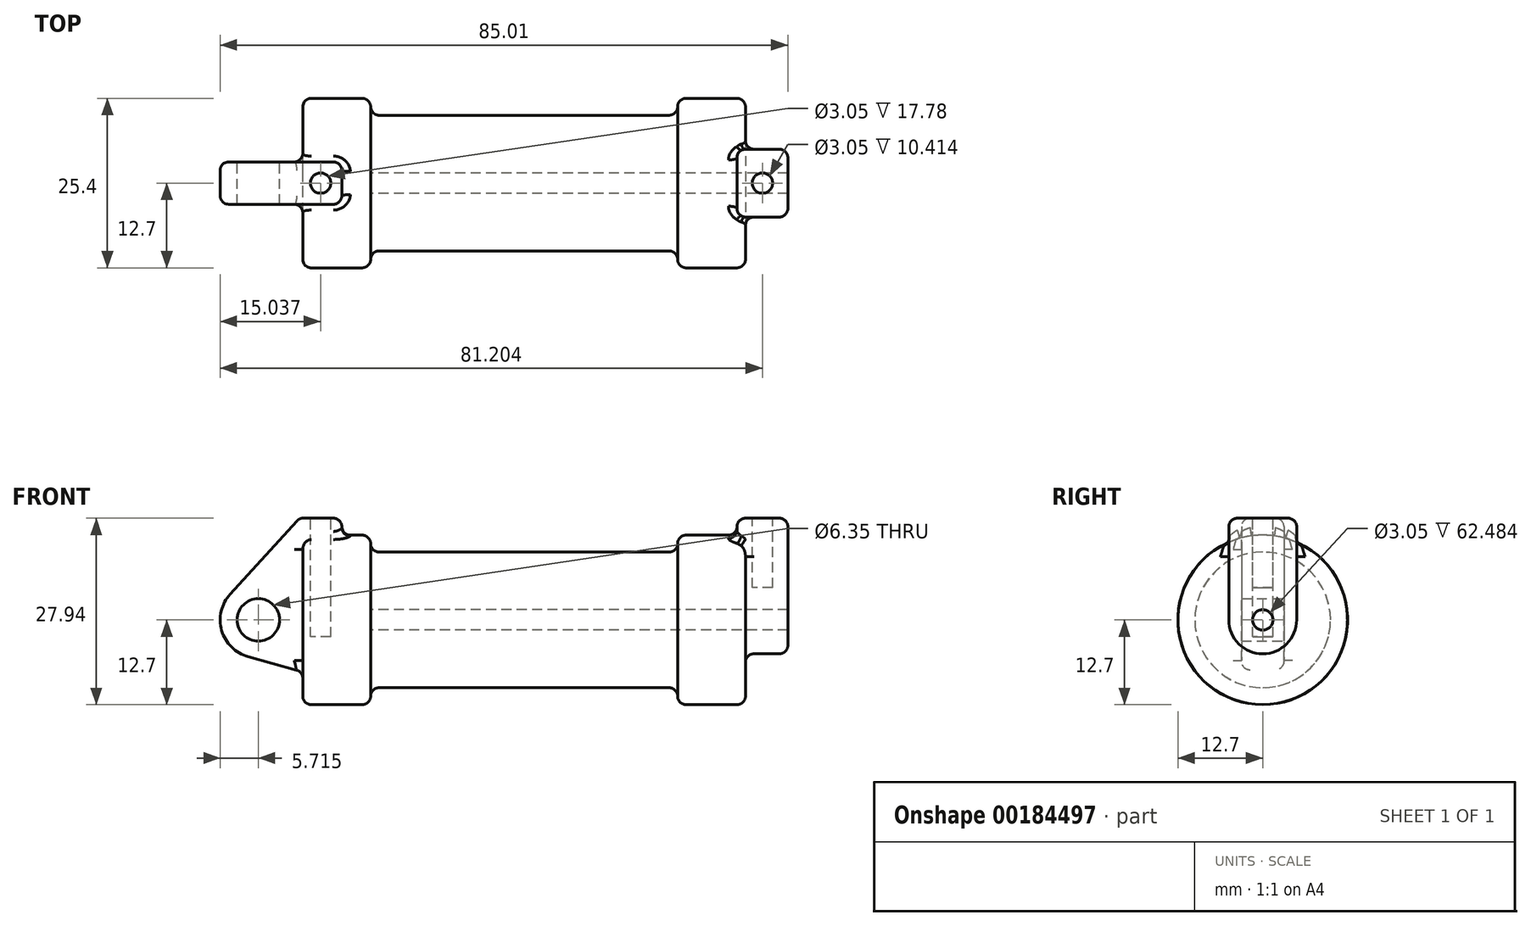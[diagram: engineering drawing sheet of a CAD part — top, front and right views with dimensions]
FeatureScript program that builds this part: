
annotation { "Feature Type Name" : "Feature", "Feature Type Description" : "" }
export const myFeature = defineFeature(function(context is Context, id is Id, definition is map)
    precondition{}
    {
        {
            var Q0;
            Q0=qCreatedBy(makeId("Front.planeOp"),FACE);
            var sketch = newSketch(context, id + "F0", { "sketchPlane" : qUnion([Q0])});
            skLineSegment(sketch, "E0", {"start": v(0, 0) * mm, "end": v(0, 12.7) * mm});
            skLineSegment(sketch, "E1", {"start": v(0, 12.7) * mm, "end": v(10.16, 12.7) * mm});
            skLineSegment(sketch, "E2", {"start": v(10.16, 12.7) * mm, "end": v(10.16, 10.16) * mm});
            skLineSegment(sketch, "E3", {"start": v(10.16, 10.16) * mm, "end": v(56.13, 10.16) * mm});
            skLineSegment(sketch, "E4", {"start": v(56.13, 10.16) * mm, "end": v(56.13, 12.7) * mm});
            skLineSegment(sketch, "E5", {"start": v(56.13, 12.7) * mm, "end": v(66.3, 12.7) * mm});
            skLineSegment(sketch, "E6", {"start": v(66.3, 12.7) * mm, "end": v(66.3, 0) * mm});
            skLineSegment(sketch, "E7", {"start": v(66.3, 0) * mm, "end": v(0, 0) * mm});
            skLineSegment(sketch, "E8", {"start": v(5.84, 15.24) * mm, "end": v(-0.5, 15.24) * mm});
            skLineSegment(sketch, "E9", {"start": v(-0.5, 15.24) * mm, "end": v(-10.88, 3.85) * mm});
            skLineSegment(sketch, "E10", {"start": v(0, 0) * mm, "end": v(-6.65, 0) * mm});
            skCircle(sketch, "E11", {"center": v(-6.65, 0) * mm, "radius": 5.72 * mm});
            skCircle(sketch, "E12", {"center": v(-6.65, 0) * mm, "radius": 3.18 * mm});
            skLineSegment(sketch, "E13", {"start": v(5.84, 15.24) * mm, "end": v(5.84, -9.4) * mm});
            skLineSegment(sketch, "E14", {"start": v(5.84, -9.4) * mm, "end": v(-8.18, -5.5) * mm});
            skSolve(sketch);
        }
        {
            var Q0;
            {var subQ0=sQuery(id+"F0.wireOp",EDGE,"E2");Q0=makeQuery(id+"F0.imprint","IMPRINT",FACE,{"disambiguationData":[TD([[makeQuery(id+"F0.imprint","IMPRINT",EDGE,{"derivedFrom":subQ0}),-1.0]])]});}
            var Q1;
            {var subQ0=sQuery(id+"F0.wireOp",EDGE,"E0");Q1=makeQuery(id+"F0.imprint","IMPRINT",FACE,{"disambiguationData":[TD([[makeQuery(id+"F0.imprint","IMPRINT",EDGE,{"derivedFrom":subQ0}),-1.0]])]});}
            var Q2;
            Q2=sQuery(id+"F0.wireOp",EDGE,"E7");
            revolve(context, id + "F1", {"entities" : qUnion([Q0, Q1]), "axis" : qUnion([Q2]), "revolveType" : RevolveType.FULL});
        }
        {
            var Q0;
            {var subQ0=sQuery(id+"F0.wireOp",EDGE,"E0");Q0=makeQuery(id+"F0.imprint","IMPRINT",FACE,{"disambiguationData":[TD([[makeQuery(id+"F0.imprint","IMPRINT",EDGE,{"derivedFrom":subQ0}),-1.0]])]});}
            var Q1;
            {var subQ3=sQuery(id+"F0.wireOp",EDGE,"E0");Q1=makeQuery(id+"F0.imprint","IMPRINT",FACE,{"disambiguationData":[TD([[makeQuery(id+"F0.imprint","IMPRINT",EDGE,{"derivedFrom":subQ3}),1.0]])]});}
            var Q2;
            {var subQ0=sQuery(id+"F0.wireOp",EDGE,"E14");Q2=makeQuery(id+"F0.imprint","IMPRINT",FACE,{"disambiguationData":[TD([[makeQuery(id+"F0.imprint","IMPRINT",EDGE,{"derivedFrom":subQ0}),-1.0]])]});}
            var Q3;
            {var subQ4=sQuery(id+"F0.wireOp",EDGE,"E12");Q3=makeQuery(id+"F0.imprint","IMPRINT",FACE,{"disambiguationData":[TD([[makeQuery(id+"F0.imprint","IMPRINT",EDGE,{"derivedFrom":subQ4}),-1.0]])]});}
            extrude(context, id + "F2", {"entities" : qUnion([Q0, Q1, Q2, Q3]), "operationType" : NewBodyOperationType.ADD, "endBound" : BoundingType.SYMMETRIC, "depth" : 6.35 * mm});
        }
        {
            var Q0;
            Q0=makeQuery(id+"F1.opRevolve","SWEPT_FACE",FACE,{"disambiguationData":[OSD([sQuery(id+"F0.wireOp",EDGE,"E6")])]});
            var sketch = newSketch(context, id + "F3", { "sketchPlane" : qUnion([Q0])});
            skCircle(sketch, "E15", {"center": v(0, 0) * mm, "radius": 1.52 * mm});
            skCircle(sketch, "E16", {"center": v(0, 0) * mm, "radius": 5.08 * mm});
            skLineSegment(sketch, "E17", {"start": v(-5.08, 0) * mm, "end": v(-5.08, 15.24) * mm});
            skLineSegment(sketch, "E18", {"start": v(5.08, 0) * mm, "end": v(5.08, 15.24) * mm});
            skLineSegment(sketch, "E19", {"start": v(5.08, 15.24) * mm, "end": v(-5.08, 15.24) * mm});
            skSolve(sketch);
        }
        {
            var Q0;
            Q0 = qSketchRegion(id + "F3", true);
            var Q1;
            Q1=makeQuery(id+"F3.imprint","IMPRINT",FACE,{"disambiguationData":[TD([[makeQuery(id+"F3.imprint","IMPRINT",EDGE,{"derivedFrom":sQuery(id+"F3.wireOp",EDGE,"E15")}),1.0]])]});
            extrude(context, id + "F4", {"entities" : qUnion([Q0, Q1]), "operationType" : NewBodyOperationType.ADD, "depth" : 6.35 * mm, "hasSecondDirection" : true, "secondDirectionOppositeDirection" : true, "secondDirectionDepth" : 1.27 * mm});
        }
        {
            var Q0;
            Q0=makeQuery(id+"F3.imprint","IMPRINT",FACE,{"disambiguationData":[TD([[makeQuery(id+"F3.imprint","IMPRINT",EDGE,{"derivedFrom":sQuery(id+"F3.wireOp",EDGE,"E15")}),1.0]])]});
            var Q1;
            Q1=makeQuery(id+"F1.opRevolve","SWEPT_FACE",FACE,{"disambiguationData":[OSD([sQuery(id+"F0.wireOp",EDGE,"E2")])]});
            extrude(context, id + "F5", {"entities" : qUnion([Q0]), "operationType" : NewBodyOperationType.REMOVE, "endBound" : BoundingType.UP_TO_NEXT, "depth" : 25.4 * mm, "hasSecondDirection" : true, "secondDirectionBound" : SecondDirectionBoundingType.UP_TO_SURFACE, "secondDirectionOppositeDirection" : true, "secondDirectionBoundEntityFace" : qUnion([Q1]), "secondDirectionDepth" : 25.4 * mm});
        }
        {
            var Q0;
            Q0=makeQuery(id+"F4.opExtrude","SWEPT_FACE",FACE,{"disambiguationData":[OSD([sQuery(id+"F3.wireOp",EDGE,"E19")])]});
            var sketch = newSketch(context, id + "F6", { "sketchPlane" : qUnion([Q0])});
            skLineSegment(sketch, "E20", {"start": v(65.02, -5.08) * mm, "end": v(72.64, 5.08) * mm, "construction": true});
            skCircle(sketch, "E21", {"center": v(68.83, 0) * mm, "radius": 1.52 * mm});
            skSolve(sketch);
        }
        {
            var Q0;
            Q0=makeQuery(id+"F2.opExtrude","SWEPT_FACE",FACE,{"disambiguationData":[OSD([sQuery(id+"F0.wireOp",EDGE,"E8")])]});
            var sketch = newSketch(context, id + "F7", { "sketchPlane" : qUnion([Q0])});
            skLineSegment(sketch, "E22", {"start": v(-0.5, 3.18) * mm, "end": v(5.84, -3.18) * mm, "construction": true});
            skCircle(sketch, "E23", {"center": v(2.67, 0) * mm, "radius": 1.52 * mm});
            skSolve(sketch);
        }
        {
            var Q0;
            Q0=makeQuery(id+"F7.imprint","IMPRINT",FACE,{"disambiguationData":[TD([[makeQuery(id+"F7.imprint","IMPRINT",EDGE,{"derivedFrom":sQuery(id+"F7.wireOp",EDGE,"E23")}),1.0]])]});
            extrude(context, id + "F8", {"entities" : qUnion([Q0]), "operationType" : NewBodyOperationType.REMOVE, "oppositeDirection" : true, "depth" : 17.78 * mm});
        }
        {
            var Q0;
            Q0=makeQuery(id+"F6.imprint","IMPRINT",FACE,{"disambiguationData":[TD([[makeQuery(id+"F6.imprint","IMPRINT",EDGE,{"derivedFrom":sQuery(id+"F6.wireOp",EDGE,"E21")}),1.0]])]});
            extrude(context, id + "F9", {"entities" : qUnion([Q0]), "operationType" : NewBodyOperationType.REMOVE, "oppositeDirection" : true, "depth" : 10.4 * mm});
        }
        {
            var Q0;
            Q0=makeQuery(id+"F1.opRevolve","SWEPT_EDGE",EDGE,{"disambiguationData":[OSD([sQuery(id+"F0.wireOp",EDGE,"E0"),sQuery(id+"F0.wireOp",EDGE,"E1")])]});
            var Q1;
            Q1=makeQuery(id+"F1.opRevolve","SWEPT_EDGE",EDGE,{"disambiguationData":[OSD([sQuery(id+"F0.wireOp",EDGE,"E1"),sQuery(id+"F0.wireOp",EDGE,"E2")])]});
            var Q2;
            Q2=makeQuery(id+"F1.opRevolve","SWEPT_EDGE",EDGE,{"disambiguationData":[OSD([sQuery(id+"F0.wireOp",EDGE,"E2"),sQuery(id+"F0.wireOp",EDGE,"E3")])]});
            var Q3;
            Q3=makeQuery(id+"F1.opRevolve","SWEPT_EDGE",EDGE,{"disambiguationData":[OSD([sQuery(id+"F0.wireOp",EDGE,"E3"),sQuery(id+"F0.wireOp",EDGE,"E4")])]});
            var Q4;
            Q4=makeQuery(id+"F1.opRevolve","SWEPT_EDGE",EDGE,{"disambiguationData":[OSD([sQuery(id+"F0.wireOp",EDGE,"E4"),sQuery(id+"F0.wireOp",EDGE,"E5")])]});
            var Q5;
            Q5=makeQuery(id+"F1.opRevolve","SWEPT_EDGE",EDGE,{"disambiguationData":[OSD([sQuery(id+"F0.wireOp",EDGE,"E5"),sQuery(id+"F0.wireOp",EDGE,"E6")])]});
            fillet(context, id + "F10", {"entities" : qUnion([Q0, Q1, Q2, Q3, Q4, Q5]), "radius" : 1.27 * mm, "tangentPropagation" : true, "allowEdgeOverflow" : false});
        }
        {
            var Q0;
            Q0=makeQuery(id+"F2.opExtrude","CAP_EDGE",EDGE,{"disambiguationData":[OSD([sQuery(id+"F0.wireOp",EDGE,"E13")])],"isStart":true});
            var Q1;
            Q1=makeQuery(id+"F2.opExtrude","CAP_EDGE",EDGE,{"disambiguationData":[OSD([sQuery(id+"F0.wireOp",EDGE,"E13")])],"isStart":false});
            var Q2;
            Q2=makeQuery(id+"F2.opExtrude","SWEPT_EDGE",EDGE,{"disambiguationData":[OSD([sQuery(id+"F0.wireOp",EDGE,"E8"),sQuery(id+"F0.wireOp",EDGE,"E9")])]});
            fillet(context, id + "F11", {"entities" : qUnion([Q0, Q1, Q2]), "radius" : 1.27 * mm, "tangentPropagation" : true, "allowEdgeOverflow" : false});
        }
        {
            var Q0;
            Q0=makeQuery(id+"F2.opExtrude","CAP_EDGE",EDGE,{"disambiguationData":[OSD([sQuery(id+"F0.wireOp",EDGE,"E14")])],"isStart":true});
            fillet(context, id + "F12", {"entities" : qUnion([Q0]), "radius" : 1.27 * mm, "tangentPropagation" : true, "allowEdgeOverflow" : false});
        }
        {
            var Q0;
            Q0=makeQuery(id+"F2.boolean.opBoolean","INTERSECT",EDGE,{"derivedFrom":[makeQuery(id+"F1.opRevolve","SWEPT_FACE",FACE,{"disambiguationData":[OSD([sQuery(id+"F0.wireOp",EDGE,"E0")])]}),makeQuery(id+"F2.opExtrude","CAP_FACE",FACE,{"disambiguationData":[OSD([sQuery(id+"F0.wireOp",EDGE,"E8"),sQuery(id+"F0.wireOp",EDGE,"E9"),sQuery(id+"F0.wireOp",EDGE,"E11"),sQuery(id+"F0.wireOp",EDGE,"E12"),sQuery(id+"F0.wireOp",EDGE,"E13"),sQuery(id+"F0.wireOp",EDGE,"E14")])],"isStart":true})]});
            fillet(context, id + "F13", {"entities" : qUnion([Q0]), "radius" : 1.27 * mm, "tangentPropagation" : true, "allowEdgeOverflow" : false});
        }
        {
            var Q0;
            Q0=makeQuery(id+"F4.opExtrude","CAP_EDGE",EDGE,{"disambiguationData":[OSD([sQuery(id+"F3.wireOp",EDGE,"E18")])],"isStart":false});
            var Q1;
            Q1=makeQuery(id+"F4.opExtrude","CAP_EDGE",EDGE,{"disambiguationData":[OSD([sQuery(id+"F3.wireOp",EDGE,"E18")])],"isStart":true});
            var Q2;
            Q2=makeQuery(id+"F4.opExtrude","CAP_EDGE",EDGE,{"disambiguationData":[OSD([sQuery(id+"F3.wireOp",EDGE,"E17")])],"isStart":true});
            fillet(context, id + "F14", {"entities" : qUnion([Q0, Q1, Q2]), "radius" : 1.27 * mm, "tangentPropagation" : true, "allowEdgeOverflow" : false});
        }
        {
            var Q0;
            Q0=makeQuery(id+"F4.boolean.opBoolean","INTERSECT",EDGE,{"derivedFrom":[makeQuery(id+"F1.opRevolve","SWEPT_FACE",FACE,{"disambiguationData":[OSD([sQuery(id+"F0.wireOp",EDGE,"E6")])]}),makeQuery(id+"F4.opExtrude","SWEPT_FACE",FACE,{"disambiguationData":[OSD([sQuery(id+"F3.wireOp",EDGE,"E17")])]})]});
            var Q1;
            Q1=makeQuery(id+"F4.opExtrude","SWEPT_EDGE",EDGE,{"disambiguationData":[OSD([sQuery(id+"F3.wireOp",EDGE,"E17"),sQuery(id+"F3.wireOp",EDGE,"E19")])]});
            fillet(context, id + "F15", {"entities" : qUnion([Q0, Q1]), "radius" : 1.27 * mm, "tangentPropagation" : true, "allowEdgeOverflow" : false});
        }
    });
